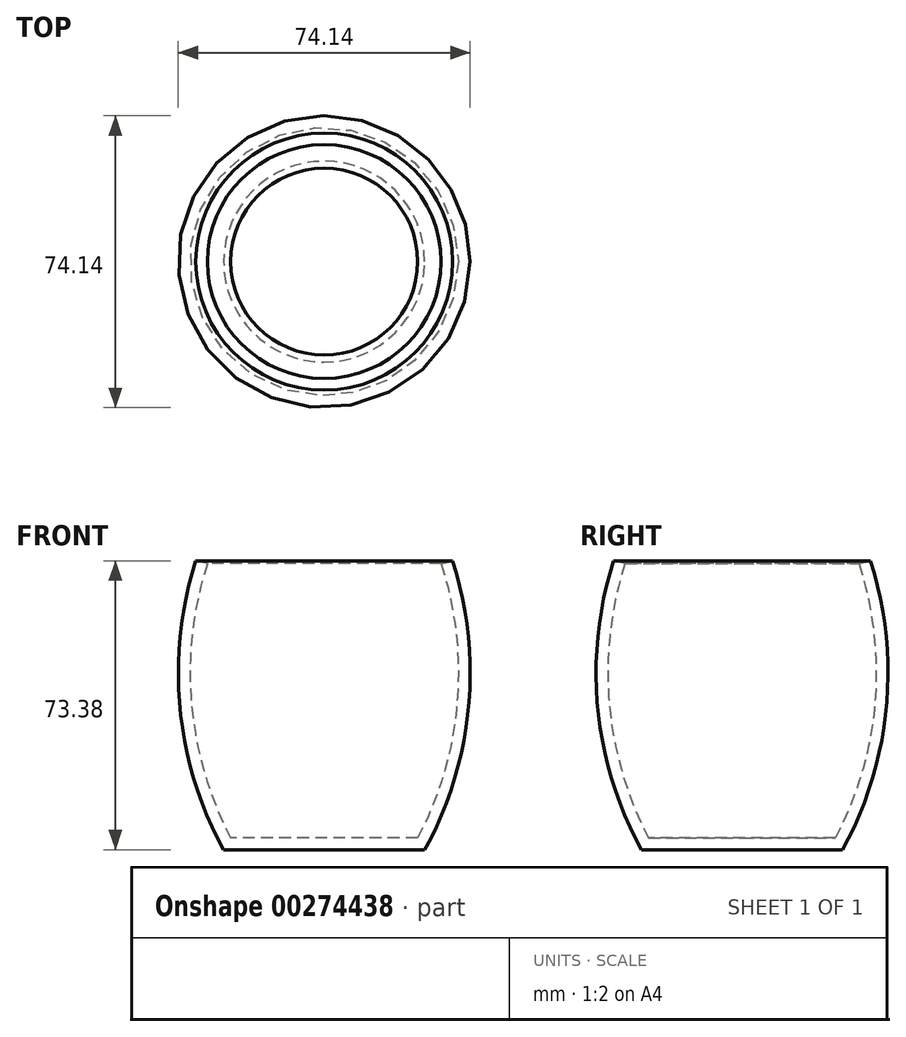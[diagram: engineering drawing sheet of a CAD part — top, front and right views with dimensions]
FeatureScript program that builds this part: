
annotation { "Feature Type Name" : "Feature", "Feature Type Description" : "" }
export const myFeature = defineFeature(function(context is Context, id is Id, definition is map)
    precondition{}
    {
        {
            var Q0;
            Q0=qCreatedBy(makeId("Front.planeOp"),FACE);
            var sketch = newSketch(context, id + "F0", { "sketchPlane" : qUnion([Q0])});
            skLineSegment(sketch, "E0", {"start": v(0, 0) * mm, "end": v(23.74, 0) * mm});
            skArc(sketch, "E1", {"start": v(23.74, 0) * mm, "mid": v(33.74, 34.27) * mm, "end": v(29.69, 69.75) * mm});
            skArc(sketch, "E2.0", {"start": v(25.53, -3) * mm, "mid": v(36.64, 32.96) * mm, "end": v(32.64, 70.38) * mm});
            skLineSegment(sketch, "E2.1", {"start": v(0, -3) * mm, "end": v(25.53, -3) * mm});
            skLineSegment(sketch, "E3", {"start": v(29.69, 69.75) * mm, "end": v(32.64, 70.38) * mm});
            skLineSegment(sketch, "E4", {"start": v(0, 0) * mm, "end": v(0, -3) * mm});
            skSolve(sketch);
        }
        {
            var Q0;
            Q0 = qSketchRegion(id + "F0", true);
            var Q1;
            Q1=sQuery(id+"F0.wireOp",EDGE,"E4");
            revolve(context, id + "F1", {"entities" : qUnion([Q0]), "axis" : qUnion([Q1]), "revolveType" : RevolveType.FULL});
        }
    });
